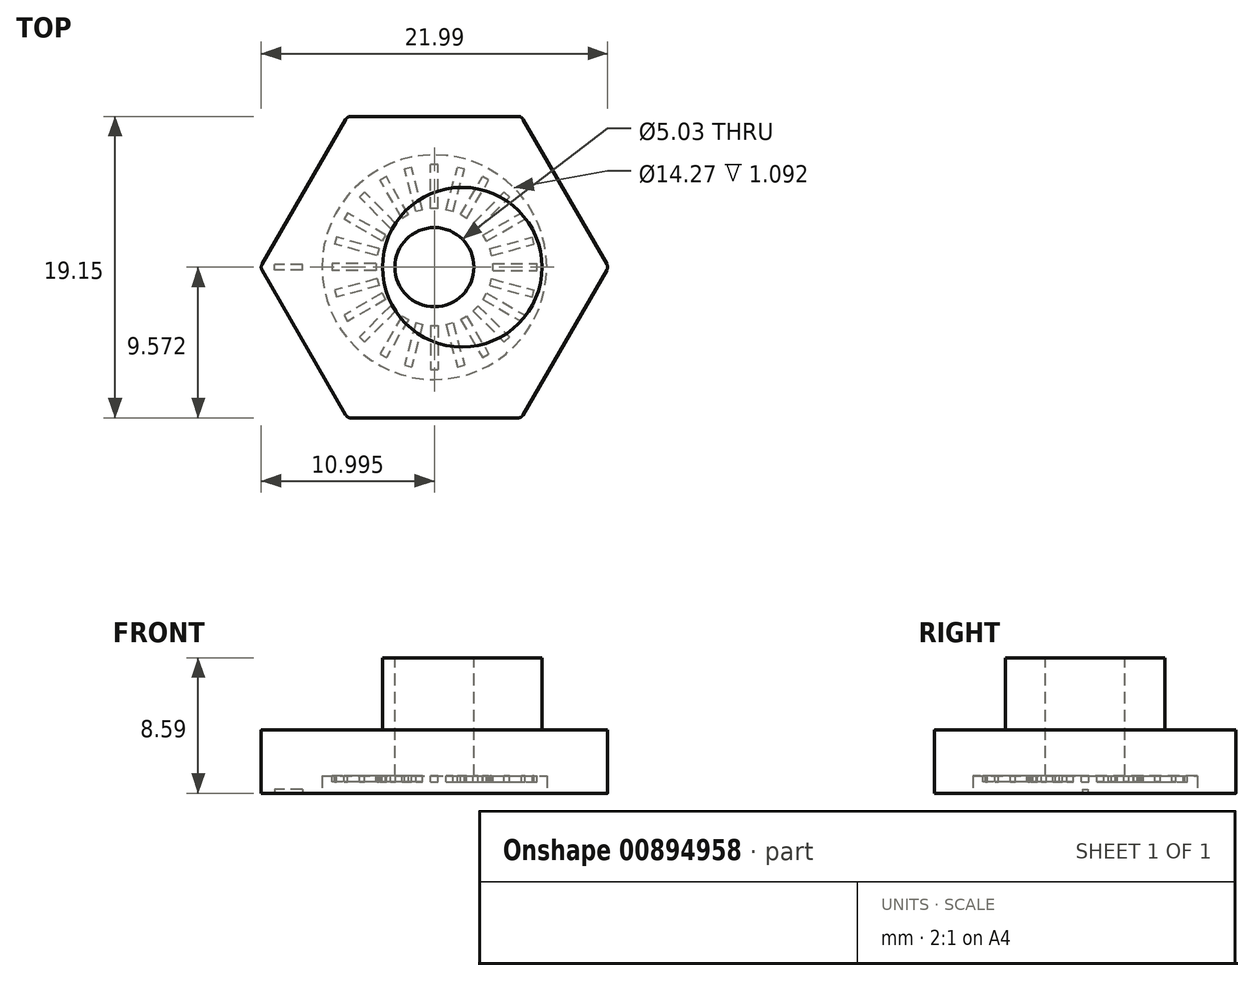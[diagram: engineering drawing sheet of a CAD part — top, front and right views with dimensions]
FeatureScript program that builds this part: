
annotation { "Feature Type Name" : "Feature", "Feature Type Description" : "" }
export const myFeature = defineFeature(function(context is Context, id is Id, definition is map)
    precondition{}
    {
        {
            var Q0;
            Q0=qCreatedBy(makeId("Top.planeOp"),FACE);
            var sketch = newSketch(context, id + "F0", { "sketchPlane" : qUnion([Q0])});
            skCircle(sketch, "E0.cCircle", {"center": v(-12.65, 2.68) * mm, "radius": 9.58 * mm, "construction": true});
            skLineSegment(sketch, "E0.0", {"start": v(-18.18, 12.26) * mm, "end": v(-7.13, 12.26) * mm});
            skLineSegment(sketch, "E0.1", {"start": v(-7.13, 12.26) * mm, "end": v(-1.6, 2.68) * mm});
            skLineSegment(sketch, "E0.2", {"start": v(-1.6, 2.68) * mm, "end": v(-7.13, -6.9) * mm});
            skLineSegment(sketch, "E0.3", {"start": v(-7.13, -6.9) * mm, "end": v(-18.18, -6.9) * mm});
            skLineSegment(sketch, "E0.4", {"start": v(-18.18, -6.9) * mm, "end": v(-23.71, 2.68) * mm});
            skLineSegment(sketch, "E0.5", {"start": v(-23.71, 2.68) * mm, "end": v(-18.18, 12.26) * mm});
            skPoint(sketch, "E0.0.midPoint", {"position": v(-12.65, 12.26) * mm});
            skSolve(sketch);
        }
        {
            var Q0;
            Q0 = qSketchRegion(id + "F0", true);
            extrude(context, id + "F1", {"entities" : qUnion([Q0]), "depth" : 4 * mm, "offsetDistance" : 25.4 * mm});
        }
        {
            var Q0;
            Q0=makeQuery(id+"F1.opExtrude","CAP_FACE",FACE,{"disambiguationData":[OSD([sQuery(id+"F0.wireOp",EDGE,"E0.0"),sQuery(id+"F0.wireOp",EDGE,"E0.1"),sQuery(id+"F0.wireOp",EDGE,"E0.2"),sQuery(id+"F0.wireOp",EDGE,"E0.3"),sQuery(id+"F0.wireOp",EDGE,"E0.4"),sQuery(id+"F0.wireOp",EDGE,"E0.5")])],"isStart":false});
            var sketch = newSketch(context, id + "F2", { "sketchPlane" : qUnion([Q0])});
            skCircle(sketch, "E1", {"center": v(-12.65, 2.68) * mm, "radius": 2.51 * mm});
            skLineSegment(sketch, "E2", {"start": v(-12.65, 2.68) * mm, "end": v(-23.71, 2.68) * mm, "construction": true});
            skLineSegment(sketch, "E3", {"start": v(-23.71, 2.68) * mm, "end": v(-1.6, 2.68) * mm, "construction": true});
            skSolve(sketch);
        }
        {
            var Q0;
            Q0 = qSketchRegion(id + "F2", true);
            extrude(context, id + "F3", {"entities" : qUnion([Q0]), "operationType" : NewBodyOperationType.REMOVE, "oppositeDirection" : true, "depth" : 25.4 * mm, "offsetDistance" : 25.4 * mm});
        }
        {
            var Q0;
            Q0=makeQuery(id+"F1.opExtrude","CAP_FACE",FACE,{"disambiguationData":[OSD([sQuery(id+"F0.wireOp",EDGE,"E0.0"),sQuery(id+"F0.wireOp",EDGE,"E0.1"),sQuery(id+"F0.wireOp",EDGE,"E0.2"),sQuery(id+"F0.wireOp",EDGE,"E0.3"),sQuery(id+"F0.wireOp",EDGE,"E0.4"),sQuery(id+"F0.wireOp",EDGE,"E0.5")])],"isStart":false});
            var sketch = newSketch(context, id + "F4", { "sketchPlane" : qUnion([Q0])});
            skCircle(sketch, "E4", {"center": v(-10.89, 2.68) * mm, "radius": 5.07 * mm});
            skLineSegment(sketch, "E5", {"start": v(-5.82, 2.68) * mm, "end": v(-10.14, 2.68) * mm, "construction": true});
            skLineSegment(sketch, "E6", {"start": v(-15.17, 2.68) * mm, "end": v(-15.96, 2.68) * mm, "construction": true});
            skCircle(sketch, "E7.0", {"center": v(-12.65, 2.68) * mm, "radius": 2.51 * mm});
            skSolve(sketch);
        }
        {
            var Q0;
            Q0 = qSketchRegion(id + "F4", true);
            extrude(context, id + "F5", {"entities" : qUnion([Q0]), "operationType" : NewBodyOperationType.ADD, "depth" : 4.57 * mm, "offsetDistance" : 25.4 * mm});
        }
        {
            var Q0;
            Q0=makeQuery(id+"F1.opExtrude","CAP_FACE",FACE,{"disambiguationData":[OSD([sQuery(id+"F0.wireOp",EDGE,"E0.0"),sQuery(id+"F0.wireOp",EDGE,"E0.1"),sQuery(id+"F0.wireOp",EDGE,"E0.2"),sQuery(id+"F0.wireOp",EDGE,"E0.3"),sQuery(id+"F0.wireOp",EDGE,"E0.4"),sQuery(id+"F0.wireOp",EDGE,"E0.5")])],"isStart":true});
            var sketch = newSketch(context, id + "F6", { "sketchPlane" : qUnion([Q0])});
            skCircle(sketch, "E8", {"center": v(-12.65, -2.68) * mm, "radius": 7.14 * mm});
            skSolve(sketch);
        }
        {
            var Q0;
            Q0 = qSketchRegion(id + "F6", true);
            extrude(context, id + "F7", {"entities" : qUnion([Q0]), "operationType" : NewBodyOperationType.REMOVE, "oppositeDirection" : true, "depth" : 1.1 * mm, "offsetDistance" : 25.4 * mm});
        }
        {
            var Q0;
            Q0=makeQuery(id+"F7.boolean.opBoolean","COPY",FACE,{"derivedFrom":makeQuery(id+"F7.opExtrude","CAP_FACE",FACE,{"disambiguationData":[OSD([sQuery(id+"F6.wireOp",EDGE,"E8")])],"isStart":false})});
            var sketch = newSketch(context, id + "F8", { "sketchPlane" : qUnion([Q0])});
            skLineSegment(sketch, "E9.bottom", {"start": v(-8.95, -2.45) * mm, "end": v(-6.15, -2.45) * mm});
            skLineSegment(sketch, "E9.top", {"start": v(-8.95, -2.91) * mm, "end": v(-6.15, -2.91) * mm});
            skLineSegment(sketch, "E9.left", {"start": v(-8.95, -2.45) * mm, "end": v(-8.95, -2.91) * mm});
            skLineSegment(sketch, "E9.right", {"start": v(-6.15, -2.45) * mm, "end": v(-6.15, -2.91) * mm});
            skPoint(sketch, "E9.middle", {"position": v(-7.55, -2.68) * mm});
            skLineSegment(sketch, "E10", {"start": v(-12.65, -2.68) * mm, "end": v(-7.55, -2.68) * mm, "construction": true});
            skLineSegment(sketch, "E11", {"start": v(-6.15, -2.68) * mm, "end": v(-5.52, -2.68) * mm, "construction": true});
            skLineSegment(sketch, "E12.1.0", {"start": v(-9.01, -1.94) * mm, "end": v(-6.31, -1.22) * mm});
            skLineSegment(sketch, "E12.1.1", {"start": v(-9.13, -1.5) * mm, "end": v(-6.43, -0.78) * mm});
            skLineSegment(sketch, "E12.1.2", {"start": v(-9.13, -1.5) * mm, "end": v(-9.01, -1.94) * mm});
            skLineSegment(sketch, "E12.1.3", {"start": v(-6.43, -0.78) * mm, "end": v(-6.31, -1.22) * mm});
            skLineSegment(sketch, "E12.2.0", {"start": v(-9.33, -1.03) * mm, "end": v(-6.9, 0.37) * mm});
            skLineSegment(sketch, "E12.2.1", {"start": v(-9.56, -0.63) * mm, "end": v(-7.14, 0.77) * mm});
            skLineSegment(sketch, "E12.2.2", {"start": v(-9.56, -0.63) * mm, "end": v(-9.33, -1.03) * mm});
            skLineSegment(sketch, "E12.2.3", {"start": v(-7.14, 0.77) * mm, "end": v(-6.9, 0.37) * mm});
            skLineSegment(sketch, "E12.3.0", {"start": v(-9.87, -0.22) * mm, "end": v(-7.9, 1.75) * mm});
            skLineSegment(sketch, "E12.3.1", {"start": v(-10.2, 0.1) * mm, "end": v(-8.22, 2.08) * mm});
            skLineSegment(sketch, "E12.3.2", {"start": v(-10.2, 0.1) * mm, "end": v(-9.87, -0.22) * mm});
            skLineSegment(sketch, "E12.3.3", {"start": v(-8.22, 2.08) * mm, "end": v(-7.9, 1.75) * mm});
            skLineSegment(sketch, "E12.4.0", {"start": v(-10.6, 0.42) * mm, "end": v(-9.2, 2.84) * mm});
            skLineSegment(sketch, "E12.4.1", {"start": v(-11, 0.64) * mm, "end": v(-9.6, 3.06) * mm});
            skLineSegment(sketch, "E12.4.2", {"start": v(-11, 0.64) * mm, "end": v(-10.6, 0.42) * mm});
            skLineSegment(sketch, "E12.4.3", {"start": v(-9.6, 3.06) * mm, "end": v(-9.2, 2.84) * mm});
            skLineSegment(sketch, "E12.5.0", {"start": v(-11.47, 0.84) * mm, "end": v(-10.75, 3.54) * mm});
            skLineSegment(sketch, "E12.5.1", {"start": v(-11.92, 0.96) * mm, "end": v(-11.2, 3.66) * mm});
            skLineSegment(sketch, "E12.5.2", {"start": v(-11.92, 0.96) * mm, "end": v(-11.47, 0.84) * mm});
            skLineSegment(sketch, "E12.5.3", {"start": v(-11.2, 3.66) * mm, "end": v(-10.75, 3.54) * mm});
            skLineSegment(sketch, "E12.6.0", {"start": v(-12.43, 1.03) * mm, "end": v(-12.43, 3.82) * mm});
            skLineSegment(sketch, "E12.6.1", {"start": v(-12.88, 1.03) * mm, "end": v(-12.88, 3.82) * mm});
            skLineSegment(sketch, "E12.6.2", {"start": v(-12.88, 1.03) * mm, "end": v(-12.43, 1.03) * mm});
            skLineSegment(sketch, "E12.6.3", {"start": v(-12.88, 3.82) * mm, "end": v(-12.43, 3.82) * mm});
            skLineSegment(sketch, "E12.7.0", {"start": v(-13.4, 0.96) * mm, "end": v(-14.12, 3.66) * mm});
            skLineSegment(sketch, "E12.7.1", {"start": v(-13.84, 0.84) * mm, "end": v(-14.56, 3.54) * mm});
            skLineSegment(sketch, "E12.7.2", {"start": v(-13.84, 0.84) * mm, "end": v(-13.4, 0.96) * mm});
            skLineSegment(sketch, "E12.7.3", {"start": v(-14.56, 3.54) * mm, "end": v(-14.12, 3.66) * mm});
            skLineSegment(sketch, "E12.8.0", {"start": v(-14.31, 0.64) * mm, "end": v(-15.7, 3.06) * mm});
            skLineSegment(sketch, "E12.8.1", {"start": v(-14.7, 0.42) * mm, "end": v(-16.1, 2.84) * mm});
            skLineSegment(sketch, "E12.8.2", {"start": v(-14.7, 0.42) * mm, "end": v(-14.31, 0.64) * mm});
            skLineSegment(sketch, "E12.8.3", {"start": v(-16.1, 2.84) * mm, "end": v(-15.7, 3.06) * mm});
            skLineSegment(sketch, "E12.9.0", {"start": v(-15.12, 0.1) * mm, "end": v(-17.1, 2.08) * mm});
            skLineSegment(sketch, "E12.9.1", {"start": v(-15.44, -0.22) * mm, "end": v(-17.41, 1.75) * mm});
            skLineSegment(sketch, "E12.9.2", {"start": v(-15.44, -0.22) * mm, "end": v(-15.12, 0.1) * mm});
            skLineSegment(sketch, "E12.9.3", {"start": v(-17.41, 1.75) * mm, "end": v(-17.1, 2.08) * mm});
            skLineSegment(sketch, "E12.10.0", {"start": v(-15.75, -0.63) * mm, "end": v(-18.17, 0.77) * mm});
            skLineSegment(sketch, "E12.10.1", {"start": v(-15.98, -1.03) * mm, "end": v(-18.4, 0.37) * mm});
            skLineSegment(sketch, "E12.10.2", {"start": v(-15.98, -1.03) * mm, "end": v(-15.75, -0.63) * mm});
            skLineSegment(sketch, "E12.10.3", {"start": v(-18.4, 0.37) * mm, "end": v(-18.17, 0.77) * mm});
            skLineSegment(sketch, "E12.11.0", {"start": v(-16.18, -1.5) * mm, "end": v(-18.88, -0.78) * mm});
            skLineSegment(sketch, "E12.11.1", {"start": v(-16.3, -1.94) * mm, "end": v(-19, -1.22) * mm});
            skLineSegment(sketch, "E12.11.2", {"start": v(-16.3, -1.94) * mm, "end": v(-16.18, -1.5) * mm});
            skLineSegment(sketch, "E12.11.3", {"start": v(-19, -1.22) * mm, "end": v(-18.88, -0.78) * mm});
            skLineSegment(sketch, "E12.12.0", {"start": v(-16.36, -2.45) * mm, "end": v(-19.16, -2.45) * mm});
            skLineSegment(sketch, "E12.12.1", {"start": v(-16.36, -2.91) * mm, "end": v(-19.16, -2.91) * mm});
            skLineSegment(sketch, "E12.12.2", {"start": v(-16.36, -2.91) * mm, "end": v(-16.36, -2.45) * mm});
            skLineSegment(sketch, "E12.12.3", {"start": v(-19.16, -2.91) * mm, "end": v(-19.16, -2.45) * mm});
            skLineSegment(sketch, "E12.13.0", {"start": v(-16.3, -3.42) * mm, "end": v(-19, -4.14) * mm});
            skLineSegment(sketch, "E12.13.1", {"start": v(-16.18, -3.86) * mm, "end": v(-18.88, -4.59) * mm});
            skLineSegment(sketch, "E12.13.2", {"start": v(-16.18, -3.86) * mm, "end": v(-16.3, -3.42) * mm});
            skLineSegment(sketch, "E12.13.3", {"start": v(-18.88, -4.59) * mm, "end": v(-19, -4.14) * mm});
            skLineSegment(sketch, "E12.14.0", {"start": v(-15.98, -4.34) * mm, "end": v(-18.4, -5.74) * mm});
            skLineSegment(sketch, "E12.14.1", {"start": v(-15.75, -4.73) * mm, "end": v(-18.17, -6.13) * mm});
            skLineSegment(sketch, "E12.14.2", {"start": v(-15.75, -4.73) * mm, "end": v(-15.98, -4.34) * mm});
            skLineSegment(sketch, "E12.14.3", {"start": v(-18.17, -6.13) * mm, "end": v(-18.4, -5.74) * mm});
            skLineSegment(sketch, "E12.15.0", {"start": v(-15.44, -5.14) * mm, "end": v(-17.41, -7.12) * mm});
            skLineSegment(sketch, "E12.15.1", {"start": v(-15.12, -5.47) * mm, "end": v(-17.1, -7.44) * mm});
            skLineSegment(sketch, "E12.15.2", {"start": v(-15.12, -5.47) * mm, "end": v(-15.44, -5.14) * mm});
            skLineSegment(sketch, "E12.15.3", {"start": v(-17.1, -7.44) * mm, "end": v(-17.41, -7.12) * mm});
            skLineSegment(sketch, "E12.16.0", {"start": v(-14.7, -5.78) * mm, "end": v(-16.1, -8.2) * mm});
            skLineSegment(sketch, "E12.16.1", {"start": v(-14.31, -6) * mm, "end": v(-15.7, -8.43) * mm});
            skLineSegment(sketch, "E12.16.2", {"start": v(-14.31, -6) * mm, "end": v(-14.7, -5.78) * mm});
            skLineSegment(sketch, "E12.16.3", {"start": v(-15.7, -8.43) * mm, "end": v(-16.1, -8.2) * mm});
            skLineSegment(sketch, "E12.17.0", {"start": v(-13.84, -6.2) * mm, "end": v(-14.56, -8.9) * mm});
            skLineSegment(sketch, "E12.17.1", {"start": v(-13.4, -6.32) * mm, "end": v(-14.12, -9.02) * mm});
            skLineSegment(sketch, "E12.17.2", {"start": v(-13.4, -6.32) * mm, "end": v(-13.84, -6.2) * mm});
            skLineSegment(sketch, "E12.17.3", {"start": v(-14.12, -9.02) * mm, "end": v(-14.56, -8.9) * mm});
            skLineSegment(sketch, "E12.18.0", {"start": v(-12.88, -6.4) * mm, "end": v(-12.88, -9.18) * mm});
            skLineSegment(sketch, "E12.18.1", {"start": v(-12.43, -6.4) * mm, "end": v(-12.43, -9.18) * mm});
            skLineSegment(sketch, "E12.18.2", {"start": v(-12.43, -6.4) * mm, "end": v(-12.88, -6.4) * mm});
            skLineSegment(sketch, "E12.18.3", {"start": v(-12.43, -9.18) * mm, "end": v(-12.88, -9.18) * mm});
            skLineSegment(sketch, "E12.19.0", {"start": v(-11.92, -6.32) * mm, "end": v(-11.2, -9.02) * mm});
            skLineSegment(sketch, "E12.19.1", {"start": v(-11.47, -6.2) * mm, "end": v(-10.75, -8.9) * mm});
            skLineSegment(sketch, "E12.19.2", {"start": v(-11.47, -6.2) * mm, "end": v(-11.92, -6.32) * mm});
            skLineSegment(sketch, "E12.19.3", {"start": v(-10.75, -8.9) * mm, "end": v(-11.2, -9.02) * mm});
            skLineSegment(sketch, "E12.20.0", {"start": v(-11, -6) * mm, "end": v(-9.6, -8.43) * mm});
            skLineSegment(sketch, "E12.20.1", {"start": v(-10.6, -5.78) * mm, "end": v(-9.2, -8.2) * mm});
            skLineSegment(sketch, "E12.20.2", {"start": v(-10.6, -5.78) * mm, "end": v(-11, -6) * mm});
            skLineSegment(sketch, "E12.20.3", {"start": v(-9.2, -8.2) * mm, "end": v(-9.6, -8.43) * mm});
            skLineSegment(sketch, "E12.21.0", {"start": v(-10.2, -5.47) * mm, "end": v(-8.22, -7.44) * mm});
            skLineSegment(sketch, "E12.21.1", {"start": v(-9.87, -5.14) * mm, "end": v(-7.9, -7.12) * mm});
            skLineSegment(sketch, "E12.21.2", {"start": v(-9.87, -5.14) * mm, "end": v(-10.2, -5.47) * mm});
            skLineSegment(sketch, "E12.21.3", {"start": v(-7.9, -7.12) * mm, "end": v(-8.22, -7.44) * mm});
            skLineSegment(sketch, "E12.22.0", {"start": v(-9.56, -4.73) * mm, "end": v(-7.14, -6.13) * mm});
            skLineSegment(sketch, "E12.22.1", {"start": v(-9.33, -4.34) * mm, "end": v(-6.9, -5.74) * mm});
            skLineSegment(sketch, "E12.22.2", {"start": v(-9.33, -4.34) * mm, "end": v(-9.56, -4.73) * mm});
            skLineSegment(sketch, "E12.22.3", {"start": v(-6.9, -5.74) * mm, "end": v(-7.14, -6.13) * mm});
            skLineSegment(sketch, "E12.23.0", {"start": v(-9.13, -3.86) * mm, "end": v(-6.43, -4.59) * mm});
            skLineSegment(sketch, "E12.23.1", {"start": v(-9.01, -3.42) * mm, "end": v(-6.31, -4.14) * mm});
            skLineSegment(sketch, "E12.23.2", {"start": v(-9.01, -3.42) * mm, "end": v(-9.13, -3.86) * mm});
            skLineSegment(sketch, "E12.23.3", {"start": v(-6.31, -4.14) * mm, "end": v(-6.43, -4.59) * mm});
            skPoint(sketch, "E12.center", {"position": v(-12.65, -2.68) * mm});
            skSolve(sketch);
        }
        {
            var Q0;
            Q0 = qSketchRegion(id + "F8", true);
            extrude(context, id + "F9", {"entities" : qUnion([Q0]), "operationType" : NewBodyOperationType.ADD, "depth" : 0.38 * mm, "offsetDistance" : 25.4 * mm});
        }
        {
            var Q0;
            Q0=makeQuery(id+"F1.opExtrude","SWEPT_EDGE",EDGE,{"disambiguationData":[OSD([sQuery(id+"F0.wireOp",EDGE,"E0.0"),sQuery(id+"F0.wireOp",EDGE,"E0.1")])]});
            var Q1;
            Q1=makeQuery(id+"F1.opExtrude","SWEPT_EDGE",EDGE,{"disambiguationData":[OSD([sQuery(id+"F0.wireOp",EDGE,"E0.0"),sQuery(id+"F0.wireOp",EDGE,"E0.5")])]});
            var Q2;
            Q2=makeQuery(id+"F1.opExtrude","SWEPT_EDGE",EDGE,{"disambiguationData":[OSD([sQuery(id+"F0.wireOp",EDGE,"E0.4"),sQuery(id+"F0.wireOp",EDGE,"E0.5")])]});
            var Q3;
            Q3=makeQuery(id+"F1.opExtrude","SWEPT_EDGE",EDGE,{"disambiguationData":[OSD([sQuery(id+"F0.wireOp",EDGE,"E0.3"),sQuery(id+"F0.wireOp",EDGE,"E0.4")])]});
            var Q4;
            Q4=makeQuery(id+"F1.opExtrude","SWEPT_EDGE",EDGE,{"disambiguationData":[OSD([sQuery(id+"F0.wireOp",EDGE,"E0.2"),sQuery(id+"F0.wireOp",EDGE,"E0.3")])]});
            var Q5;
            Q5=makeQuery(id+"F1.opExtrude","SWEPT_EDGE",EDGE,{"disambiguationData":[OSD([sQuery(id+"F0.wireOp",EDGE,"E0.1"),sQuery(id+"F0.wireOp",EDGE,"E0.2")])]});
            fillet(context, id + "F10", {"entities" : qUnion([Q0, Q1, Q2, Q3, Q4, Q5]), "radius" : 0.38 * mm, "tangentPropagation" : true, "allowEdgeOverflow" : false});
        }
        {
            var Q0;
            Q0=makeQuery(id+"F1.opExtrude","CAP_FACE",FACE,{"disambiguationData":[OSD([sQuery(id+"F0.wireOp",EDGE,"E0.0"),sQuery(id+"F0.wireOp",EDGE,"E0.1"),sQuery(id+"F0.wireOp",EDGE,"E0.2"),sQuery(id+"F0.wireOp",EDGE,"E0.3"),sQuery(id+"F0.wireOp",EDGE,"E0.4"),sQuery(id+"F0.wireOp",EDGE,"E0.5")])],"isStart":true});
            var sketch = newSketch(context, id + "F11", { "sketchPlane" : qUnion([Q0])});
            skLineSegment(sketch, "E13.bottom", {"start": v(-21.04, -2.5) * mm, "end": v(-22.81, -2.5) * mm});
            skLineSegment(sketch, "E13.top", {"start": v(-21.04, -2.86) * mm, "end": v(-22.81, -2.86) * mm});
            skLineSegment(sketch, "E13.left", {"start": v(-21.04, -2.5) * mm, "end": v(-21.04, -2.86) * mm});
            skLineSegment(sketch, "E13.right", {"start": v(-22.81, -2.5) * mm, "end": v(-22.81, -2.86) * mm});
            skPoint(sketch, "E13.middle", {"position": v(-21.93, -2.68) * mm});
            skLineSegment(sketch, "E14", {"start": v(-21.93, -2.68) * mm, "end": v(-12.65, -2.68) * mm, "construction": true});
            skSolve(sketch);
        }
        {
            var Q0;
            Q0 = qSketchRegion(id + "F11", true);
            extrude(context, id + "F12", {"entities" : qUnion([Q0]), "operationType" : NewBodyOperationType.REMOVE, "oppositeDirection" : true, "depth" : 0.25 * mm, "offsetDistance" : 25.4 * mm});
        }
    });
